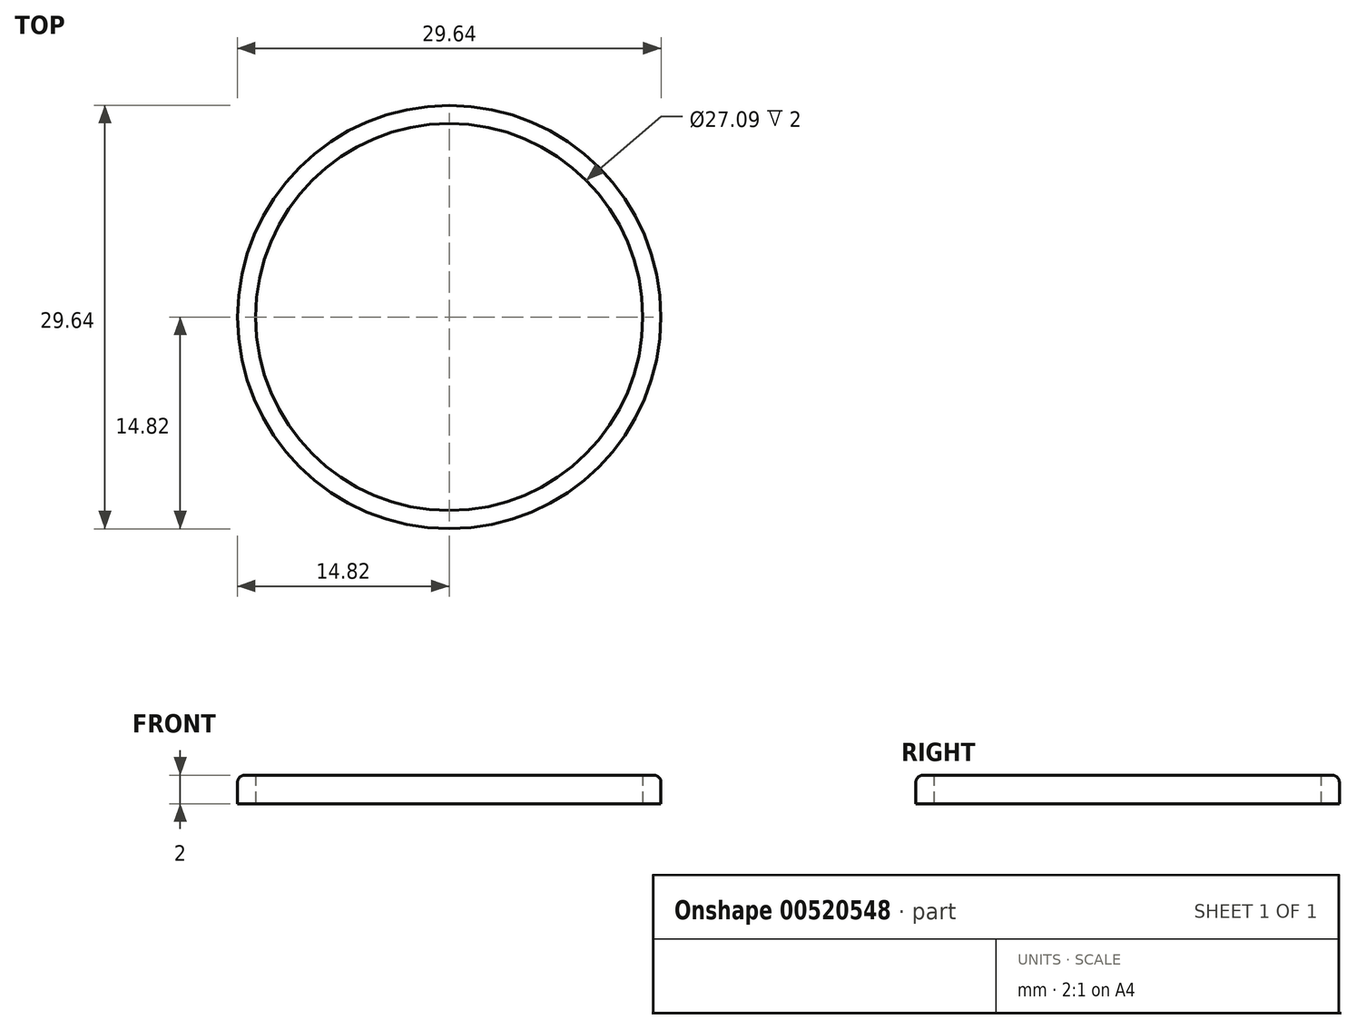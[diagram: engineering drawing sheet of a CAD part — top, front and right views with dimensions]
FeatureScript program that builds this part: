
annotation { "Feature Type Name" : "Feature", "Feature Type Description" : "" }
export const myFeature = defineFeature(function(context is Context, id is Id, definition is map)
    precondition{}
    {
        {
            var Q0;
            Q0=qCreatedBy(makeId("Top.planeOp"),FACE);
            var sketch = newSketch(context, id + "F0", { "sketchPlane" : qUnion([Q0])});
            skCircle(sketch, "E0", {"center": v(0, 0) * mm, "radius": 14.82 * mm});
            skCircle(sketch, "E1", {"center": v(0, 0) * mm, "radius": 13.54 * mm});
            skSolve(sketch);
        }
        {
            var Q0;
            Q0 = qSketchRegion(id + "F0", true);
            extrude(context, id + "F1", {"entities" : qUnion([Q0]), "depth" : 2 * mm, "offsetDistance" : 25 * mm});
        }
        {
            var Q0;
            Q0=makeQuery(id+"F1.opExtrude","CAP_EDGE",EDGE,{"disambiguationData":[OSD([sQuery(id+"F0.wireOp",EDGE,"E0")])],"isStart":false});
            fillet(context, id + "F2", {"entities" : qUnion([Q0]), "radius" : 0.5 * mm, "tangentPropagation" : true, "allowEdgeOverflow" : false});
        }
    });
